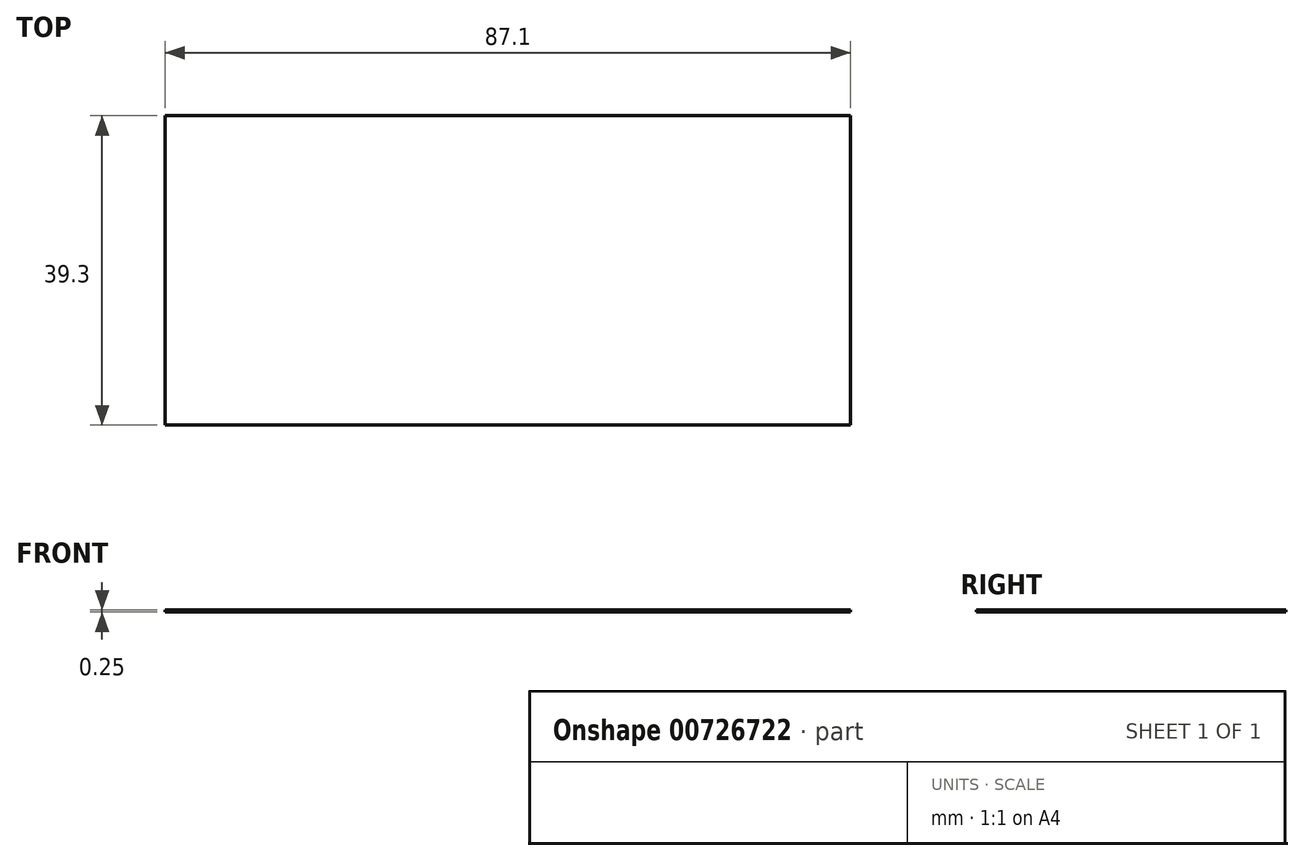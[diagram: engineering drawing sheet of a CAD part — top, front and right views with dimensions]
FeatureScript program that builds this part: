
annotation { "Feature Type Name" : "Feature", "Feature Type Description" : "" }
export const myFeature = defineFeature(function(context is Context, id is Id, definition is map)
    precondition{}
    {
        {
            var Q0;
            Q0=qCreatedBy(makeId("Front.planeOp"),FACE);
            var sketch = newSketch(context, id + "F0", { "sketchPlane" : qUnion([Q0])});
            skLineSegment(sketch, "E0.bottom", {"start": v(-20.2, 30.75) * mm, "end": v(24.24, 30.75) * mm});
            skLineSegment(sketch, "E0.top", {"start": v(-20.2, -30.75) * mm, "end": v(24.24, -30.75) * mm});
            skLineSegment(sketch, "E0.left", {"start": v(-20.2, 30.75) * mm, "end": v(-20.2, -30.75) * mm});
            skLineSegment(sketch, "E0.right", {"start": v(24.24, 30.75) * mm, "end": v(24.24, -30.75) * mm});
            skPoint(sketch, "E0.middle", {"position": v(2.02, 0) * mm});
            skSolve(sketch);
        }
        {
            var Q0;
            Q0 = qSketchRegion(id + "F0", true);
            extrude(context, id + "F1", {"entities" : qUnion([Q0]), "depth" : 2.54 * mm, "offsetDistance" : 25.4 * mm});
        }
        {
            var Q0;
            Q0=makeQuery(id+"F1.opExtrude","SWEPT_BODY",BODY,{"disambiguationData":[OSD([sQuery(id+"F0.wireOp",EDGE,"E0.bottom"),sQuery(id+"F0.wireOp",EDGE,"E0.top"),sQuery(id+"F0.wireOp",EDGE,"E0.left"),sQuery(id+"F0.wireOp",EDGE,"E0.right")])]});
            deleteBodies(context, id + "F2", {"entities" : qUnion([Q0])});
        }
        {
            var Q0;
            Q0=qCreatedBy(makeId("Top.planeOp"),FACE);
            var sketch = newSketch(context, id + "F3", { "sketchPlane" : qUnion([Q0])});
            skLineSegment(sketch, "E1.bottom", {"start": v(-43.55, -19.65) * mm, "end": v(43.55, -19.65) * mm});
            skLineSegment(sketch, "E1.top", {"start": v(-43.55, 19.65) * mm, "end": v(43.55, 19.65) * mm});
            skLineSegment(sketch, "E1.left", {"start": v(-43.55, -19.65) * mm, "end": v(-43.55, 19.65) * mm});
            skLineSegment(sketch, "E1.right", {"start": v(43.55, -19.65) * mm, "end": v(43.55, 19.65) * mm});
            skPoint(sketch, "E1.middle", {"position": v(0, 0) * mm});
            skSolve(sketch);
        }
        {
            var Q0;
            Q0 = qSketchRegion(id + "F3", true);
            extrude(context, id + "F4", {"entities" : qUnion([Q0]), "depth" : 0.25 * mm, "offsetDistance" : 25.4 * mm});
        }
    });
